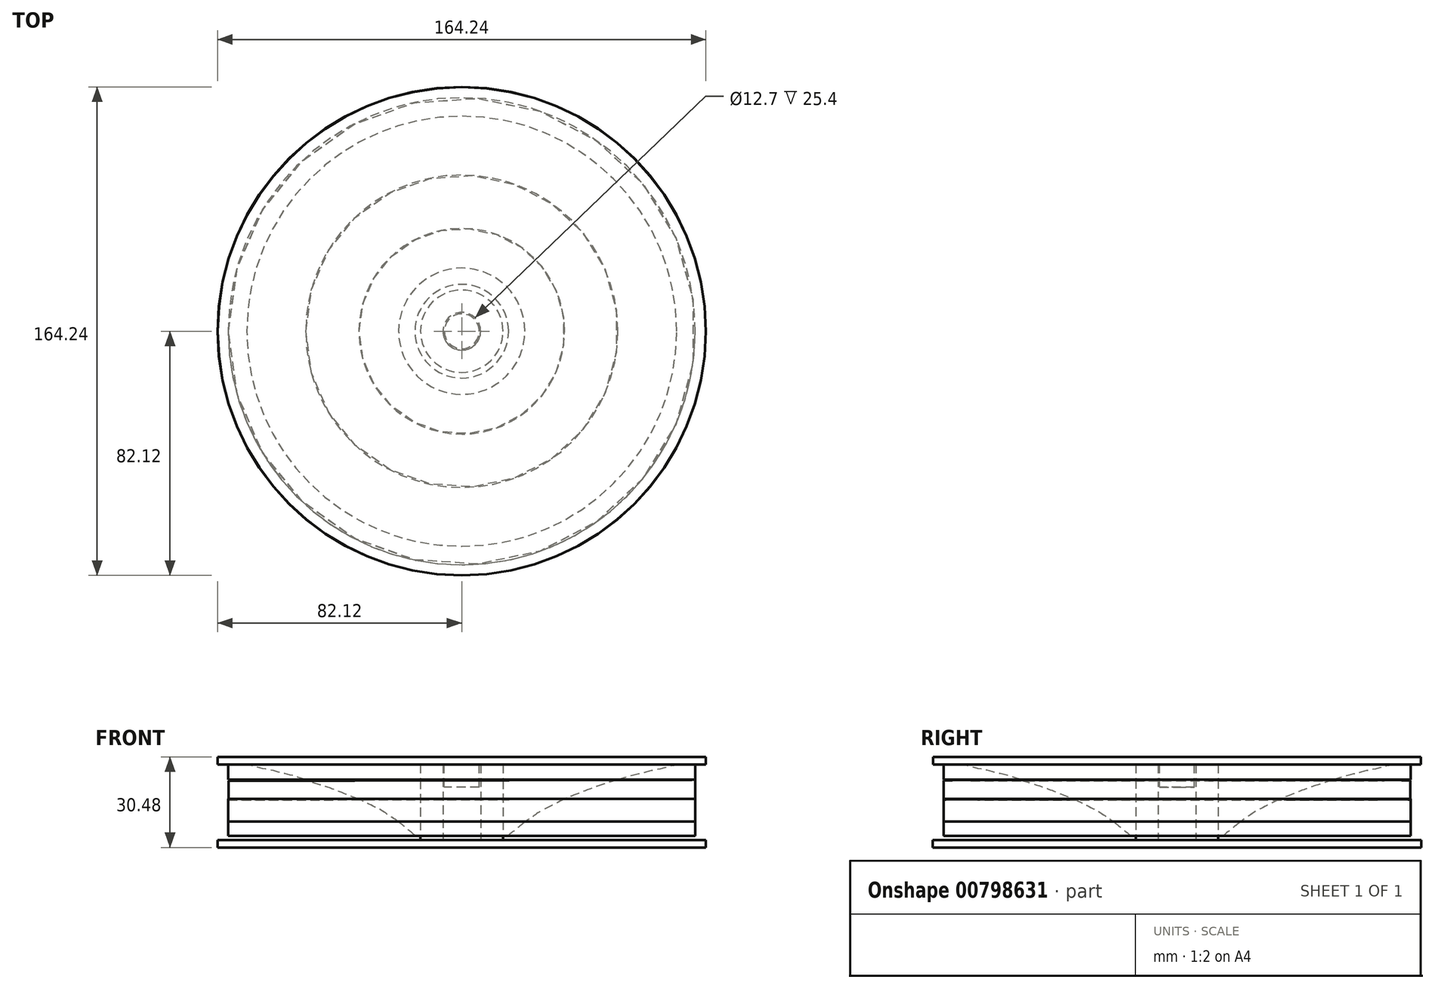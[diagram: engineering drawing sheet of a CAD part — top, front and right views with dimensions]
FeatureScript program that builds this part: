
annotation { "Feature Type Name" : "Feature", "Feature Type Description" : "" }
export const myFeature = defineFeature(function(context is Context, id is Id, definition is map)
    precondition{}
    {
        {
            var Q0;
            Q0=qCreatedBy(makeId("Front.planeOp"),FACE);
            var sketch = newSketch(context, id + "F0", { "sketchPlane" : qUnion([Q0])});
            skPoint(sketch, "E0", {"position": v(15.75, 1.52) * mm});
            skPoint(sketch, "E1", {"position": v(17.28, 2.83) * mm});
            skPoint(sketch, "E2", {"position": v(18.96, 4.19) * mm});
            skPoint(sketch, "E3", {"position": v(20.72, 5.64) * mm});
            skPoint(sketch, "E4", {"position": v(21.99, 6.59) * mm});
            skPoint(sketch, "E5", {"position": v(23.17, 7.4) * mm});
            skPoint(sketch, "E6", {"position": v(24.75, 8.44) * mm});
            skPoint(sketch, "E7", {"position": v(25.79, 9.17) * mm});
            skPoint(sketch, "E8", {"position": v(26.74, 9.75) * mm});
            skPoint(sketch, "E9", {"position": v(27.69, 10.3) * mm});
            skPoint(sketch, "E10", {"position": v(29.05, 10.98) * mm});
            skPoint(sketch, "E11", {"position": v(29.86, 11.47) * mm});
            skPoint(sketch, "E12", {"position": v(30.72, 11.79) * mm});
            skPoint(sketch, "E13", {"position": v(31.94, 12.42) * mm});
            skPoint(sketch, "E14", {"position": v(33.75, 13.28) * mm});
            skPoint(sketch, "E15", {"position": v(34.66, 13.78) * mm});
            skPoint(sketch, "E16", {"position": v(36.15, 14.46) * mm});
            skPoint(sketch, "E17", {"position": v(38, 15.14) * mm});
            skPoint(sketch, "E18", {"position": v(40, 15.95) * mm});
            skPoint(sketch, "E19", {"position": v(41.44, 16.5) * mm});
            skPoint(sketch, "E20", {"position": v(42.84, 17) * mm});
            skPoint(sketch, "E21", {"position": v(44.34, 17.63) * mm});
            skPoint(sketch, "E22", {"position": v(45.47, 18.03) * mm});
            skPoint(sketch, "E23", {"position": v(46.28, 18.26) * mm});
            skPoint(sketch, "E24", {"position": v(47.55, 18.9) * mm});
            skPoint(sketch, "E25", {"position": v(48.18, 18.98) * mm});
            skPoint(sketch, "E26", {"position": v(49.04, 19.3) * mm});
            skPoint(sketch, "E27", {"position": v(49.67, 19.34) * mm});
            skPoint(sketch, "E28", {"position": v(51.76, 20.16) * mm});
            skPoint(sketch, "E29", {"position": v(53.3, 20.48) * mm});
            skPoint(sketch, "E30", {"position": v(55.37, 20.84) * mm});
            skPoint(sketch, "E31", {"position": v(56.69, 21.6) * mm});
            skPoint(sketch, "E32", {"position": v(58.22, 21.88) * mm});
            skPoint(sketch, "E33", {"position": v(60.22, 22.42) * mm});
            skPoint(sketch, "E34", {"position": v(61.35, 22.6) * mm});
            skPoint(sketch, "E35", {"position": v(62.8, 23.14) * mm});
            skPoint(sketch, "E36", {"position": v(64.1, 23.5) * mm});
            skPoint(sketch, "E37", {"position": v(66.32, 23.87) * mm});
            skPoint(sketch, "E38", {"position": v(68.09, 24.23) * mm});
            skPoint(sketch, "E39", {"position": v(70.12, 24.82) * mm});
            skPoint(sketch, "E40", {"position": v(71.66, 25.09) * mm});
            skPoint(sketch, "E41", {"position": v(73.52, 25.68) * mm});
            skPoint(sketch, "E42", {"position": v(74.96, 25.95) * mm});
            skPoint(sketch, "E43", {"position": v(76.86, 26.18) * mm});
            skPoint(sketch, "E44", {"position": v(78.54, 26.72) * mm});
            skFitSpline(sketch, "E45", {"points": [v(15.75, 1.52) * mm, v(17.28, 2.83) * mm, v(18.96, 4.19) * mm, v(20.72, 5.64) * mm, v(21.99, 6.59) * mm, v(23.17, 7.4) * mm, v(24.75, 8.44) * mm, v(25.79, 9.17) * mm, v(29.05, 10.98) * mm, v(31.94, 12.42) * mm, v(34.66, 13.78) * mm, v(38, 15.14) * mm, v(41.44, 16.5) * mm, v(45.47, 18.03) * mm, v(49.67, 19.34) * mm, v(53.3, 20.48) * mm, v(56.69, 21.6) * mm, v(60.22, 22.42) * mm, v(62.8, 23.14) * mm, v(66.32, 23.87) * mm, v(70.12, 24.82) * mm, v(73.52, 25.68) * mm, v(76.86, 26.18) * mm, v(78.54, 26.18) * mm], "startDerivative": vector(41.71, 36.37) * mm, "endDerivative": vector(45.9, -1.96) * mm});
            skLineSegment(sketch, "E46", {"start": v(78.54, 26.18) * mm, "end": v(78.54, 1.32) * mm});
            skLineSegment(sketch, "E47", {"start": v(78.54, 1.32) * mm, "end": v(15.75, 1.52) * mm});
            skLineSegment(sketch, "E48", {"start": v(0, 1.5) * mm, "end": v(0, 31.45) * mm});
            skLineSegment(sketch, "E49", {"start": v(0, 1.5) * mm, "end": v(0.07, 1.5) * mm});
            skLineSegment(sketch, "E50", {"start": v(0.07, 1.5) * mm, "end": v(0, 31.45) * mm});
            skLineSegment(sketch, "E51", {"start": v(78.54, 6.17) * mm, "end": v(0, 5.99) * mm});
            skLineSegment(sketch, "E52", {"start": v(78.54, 13.75) * mm, "end": v(0, 13.75) * mm});
            skLineSegment(sketch, "E53", {"start": v(78.54, 20.21) * mm, "end": v(0, 20.21) * mm});
            skSolve(sketch);
        }
        {
            var Q0;
            {var subQ0=sQuery(id+"F0.wireOp",EDGE,"E47");Q0=makeQuery(id+"F0.imprint","IMPRINT",FACE,{"disambiguationData":[TD([[makeQuery(id+"F0.imprint","IMPRINT",EDGE,{"derivedFrom":subQ0}),-1.0]])]});}
            var Q1;
            Q1=sQuery(id+"F0.wireOp",EDGE,"E48");
            revolve(context, id + "F1", {"surfaceOperationType" : NewSurfaceOperationType.NEW, "entities" : qUnion([Q0]), "axis" : qUnion([Q1]), "revolveType" : RevolveType.FULL});
        }
        {
            var Q0;
            {var subQ0=sQuery(id+"F0.wireOp",EDGE,"E51");var subQ1=sQuery(id+"F0.wireOp",EDGE,"E45");var subQ2=makeQuery(id+"F0.imprint","INTERSECT",VERTEX,{"derivedFrom":[subQ1,subQ0]});Q0=makeQuery(id+"F0.imprint","IMPRINT",FACE,{"disambiguationData":[TD([[makeQuery(id+"F0.imprint","IMPRINT",EDGE,{"disambiguationData":[TD([[subQ2,-1.0]])],"derivedFrom":subQ1}),-1.0]])]});}
            var Q1;
            Q1=sQuery(id+"F0.wireOp",EDGE,"E48");
            revolve(context, id + "F2", {"surfaceOperationType" : NewSurfaceOperationType.NEW, "entities" : qUnion([Q0]), "axis" : qUnion([Q1]), "revolveType" : RevolveType.FULL});
        }
        {
            var Q0;
            {var subQ0=sQuery(id+"F0.wireOp",EDGE,"E53");var subQ1=sQuery(id+"F0.wireOp",EDGE,"E45");var subQ2=makeQuery(id+"F0.imprint","INTERSECT",VERTEX,{"derivedFrom":[subQ1,subQ0]});Q0=makeQuery(id+"F0.imprint","IMPRINT",FACE,{"disambiguationData":[TD([[makeQuery(id+"F0.imprint","IMPRINT",EDGE,{"disambiguationData":[TD([[subQ2,1.0]])],"derivedFrom":subQ1}),-1.0]])]});}
            var Q1;
            Q1=sQuery(id+"F0.wireOp",EDGE,"E50");
            revolve(context, id + "F3", {"surfaceOperationType" : NewSurfaceOperationType.NEW, "entities" : qUnion([Q0]), "axis" : qUnion([Q1]), "revolveType" : RevolveType.FULL});
        }
        {
            var Q0;
            {var subQ0=sQuery(id+"F0.wireOp",EDGE,"E46");var subQ1=sQuery(id+"F0.wireOp",EDGE,"E45");var subQ2=makeQuery(id+"F0.imprint","INTERSECT",VERTEX,{"derivedFrom":[subQ1,subQ0]});Q0=makeQuery(id+"F0.imprint","IMPRINT",FACE,{"disambiguationData":[TD([[makeQuery(id+"F0.imprint","IMPRINT",EDGE,{"disambiguationData":[TD([[subQ2,1.0]])],"derivedFrom":subQ1}),-1.0]])]});}
            var Q1;
            Q1=sQuery(id+"F0.wireOp",EDGE,"E48");
            revolve(context, id + "F4", {"surfaceOperationType" : NewSurfaceOperationType.NEW, "entities" : qUnion([Q0]), "axis" : qUnion([Q1]), "revolveType" : RevolveType.FULL});
        }
        {
            var Q0;
            Q0=qCreatedBy(makeId("Top.planeOp"),FACE);
            var sketch = newSketch(context, id + "F5", { "sketchPlane" : qUnion([Q0])});
            skCircle(sketch, "E54", {"center": v(0, 0) * mm, "radius": 13.4 * mm});
            skCircle(sketch, "E55", {"center": v(0, 0) * mm, "radius": 82.12 * mm});
            skSolve(sketch);
        }
        {
            var Q0;
            Q0=qSketchRegion(id+"F5",true);
            var Q1;
            Q1=makeQuery(id+"F5.imprint","IMPRINT",FACE,{"disambiguationData":[TD([[makeQuery(id+"F5.imprint","IMPRINT",EDGE,{"derivedFrom":sQuery(id+"F5.wireOp",EDGE,"E54")}),1.0]])]});
            extrude(context, id + "F6", {"entities" : qUnion([Q0, Q1]), "oppositeDirection" : true, "depth" : 2.54 * mm, "offsetDistance" : 25.4 * mm});
        }
        {
            var Q0;
            Q0=qCreatedBy(makeId("Top.planeOp"),FACE);
            var sketch = newSketch(context, id + "F7", { "sketchPlane" : qUnion([Q0])});
            skCircle(sketch, "E56", {"center": v(0, 0) * mm, "radius": 13.87 * mm});
            skSolve(sketch);
        }
        {
            var Q0;
            Q0=makeQuery(id+"F7.imprint","IMPRINT",FACE,{"disambiguationData":[TD([[makeQuery(id+"F7.imprint","IMPRINT",EDGE,{"derivedFrom":sQuery(id+"F7.wireOp",EDGE,"E56")}),1.0]])]});
            extrude(context, id + "F8", {"entities" : qUnion([Q0]), "operationType" : NewBodyOperationType.ADD, "depth" : 25.4 * mm, "offsetDistance" : 25.4 * mm});
        }
        {
            var Q0;
            Q0=makeQuery(id+"F8.opExtrude","CAP_FACE",FACE,{"disambiguationData":[OSD([sQuery(id+"F7.wireOp",EDGE,"E56")])],"isStart":false});
            var sketch = newSketch(context, id + "F9", { "sketchPlane" : qUnion([Q0])});
            skCircle(sketch, "E57", {"center": v(0, 0) * mm, "radius": 82.08 * mm});
            skSolve(sketch);
        }
        {
            var Q0;
            Q0=sQuery(id+"F7.wireOp",VERTEX,"E56.center");
            var Q1;
            Q1=makeQuery(id+"F6.opExtrude","SWEPT_BODY",BODY,{"disambiguationData":[OSD([sQuery(id+"F5.wireOp",EDGE,"E55")])]});
            hole(context, id + "F10", {"style" : HoleStyle.SIMPLE, "endStyle" : HoleEndStyle.THROUGH, "oppositeDirection" : true, "holeDiameter" : 12.7 * mm, "majorDiameter" : 6.35 * mm, "isTappedThrough" : true, "tappedDepth" : 12.7 * mm, "tapClearance" : 3, "locations" : qUnion([Q0]), "scope" : qUnion([Q1])});
        }
        {
            var Q0;
            Q0=makeQuery(id+"F9.imprint","IMPRINT",FACE,{"disambiguationData":[TD([[makeQuery(id+"F9.imprint","IMPRINT",EDGE,{"derivedFrom":makeQuery(id+"F8.opExtrude","CAP_EDGE",EDGE,{"disambiguationData":[OSD([sQuery(id+"F7.wireOp",EDGE,"E56")])],"isStart":false})}),1.0]])]});
            var sketch = newSketch(context, id + "F11", { "sketchPlane" : qUnion([Q0])});
            skCircle(sketch, "E58", {"center": v(0, 0) * mm, "radius": 5.86 * mm});
            skSolve(sketch);
        }
        {
            var Q0;
            Q0=qSketchRegion(id+"F11",true);
            extrude(context, id + "F12", {"entities" : qUnion([Q0]), "oppositeDirection" : true, "depth" : 7.62 * mm, "offsetDistance" : 25.4 * mm});
        }
        {
            var Q0;
            Q0=qSketchRegion(id+"F9",true);
            extrude(context, id + "F13", {"entities" : qUnion([Q0]), "operationType" : NewBodyOperationType.ADD, "depth" : 2.54 * mm, "offsetDistance" : 25.4 * mm});
        }
    });
